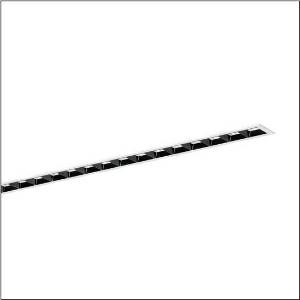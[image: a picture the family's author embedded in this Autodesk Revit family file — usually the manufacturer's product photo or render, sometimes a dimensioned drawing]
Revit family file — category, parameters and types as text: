
# Revit family: silica_r__21_51mx14da44wb_4ffe
name_source: partatom
category: Lighting Fixtures
units: mm (PartAtom-declared; Revit-internal decimal feet)

## family parameters
Cut with Voids When Loaded = No
Host = Face
Light Source = No
Part Type = Normal
Room Calculation Point = No
Round Connector Dimension = Use Diameter
Shared = No

## types (1)
- --- (1 x LED, 4320 lm, 30 W, 4000K)
    Apparent Load = 30 VA
    CIE Flux Codes = 74 94 99 100 100
    Color Rendering = 80
    Color Temperature = 4000K
    Default Elevation = 1800 mm
    Description = Silica® 21, office luminaire, primary light control with darklight reflector, of PMMA, black, light emission: direct distribution, primary light characteristic: asymmetric, installation type: recessed, LED, rated luminous flux: 4.320lm, luminous efficacy: 144lm/W, light colour: 840, colour temperature: 4000K, control gear: DALI 2, with terminal, 3+2-pole, max. 2.5mm², mains connection: 220..240V, AC, 50/60Hz, rated input power: 30W, luminaire housing, of aluminium, traffic white (RAL 9016), length: 1.228mm, width: 79mm, height: 53mm, protection rating (complete): IP20, insulation class (complete): insulation class I (protective earthing), certification: CE, ENEC, VDE, permissible operating ambient temperature: 0..+35°C, standard: EN 50419, packaging unit: 1 piece
    Height = 0 mm  [stored 0 ft]
    Lamp = 1 x LED
    Lamp Light Flux = 4320 lm
    Lamp Power = 30 W
    Lamp count = 1
    Length = 1227 mm
    Luminous efficacy = 144 lm/W
    Manufacturer = Siteco
    ModVariant = No
    Model = 51MX14DA44WB
    Mounting Place = Ceiling
    Mounting Type = Recessed
    Number of Poles = 1
    OnlyDefault = Yes
    Power Factor = 1
    Product Name = Silica® 21
    Product group = office luminaire | ceiling recessed
    ProductGroupID = 401
    Protection Class = Protection class I
    Protection Degree = IP 20
    RLX_Detail_Level = 1
    RLX_Emergency_Light_Flux = 0 lm
    RLX_Emergency_Type = 0
    RLX_Emergency_Type_DB = No
    RlxData = <blob elided: 39353 chars, md5=1d4a866c>
    Socket = socket
    Standby Power = 0 W
    System Light Flux = 4320 lm
    System Power = 30 W
    Type Comments = factory setting: luminous flux: 100 % | dim-lin: 254 | 418 mA
    Type Image = l_1335880.jpg
    URL = http://relux.com
    VarID = @adj_122530
    Voltage = 0 V
    Weight = 0.00 kg
    Width = 79 mm

note: [stored X ft] marks values corroborated as IEEE doubles in the binary element streams (Revit-internal decimal feet)

## geometry (parser evidence)
native form markers: Blend x4, Sweep x12
no freeform markers — native parametric forms only
